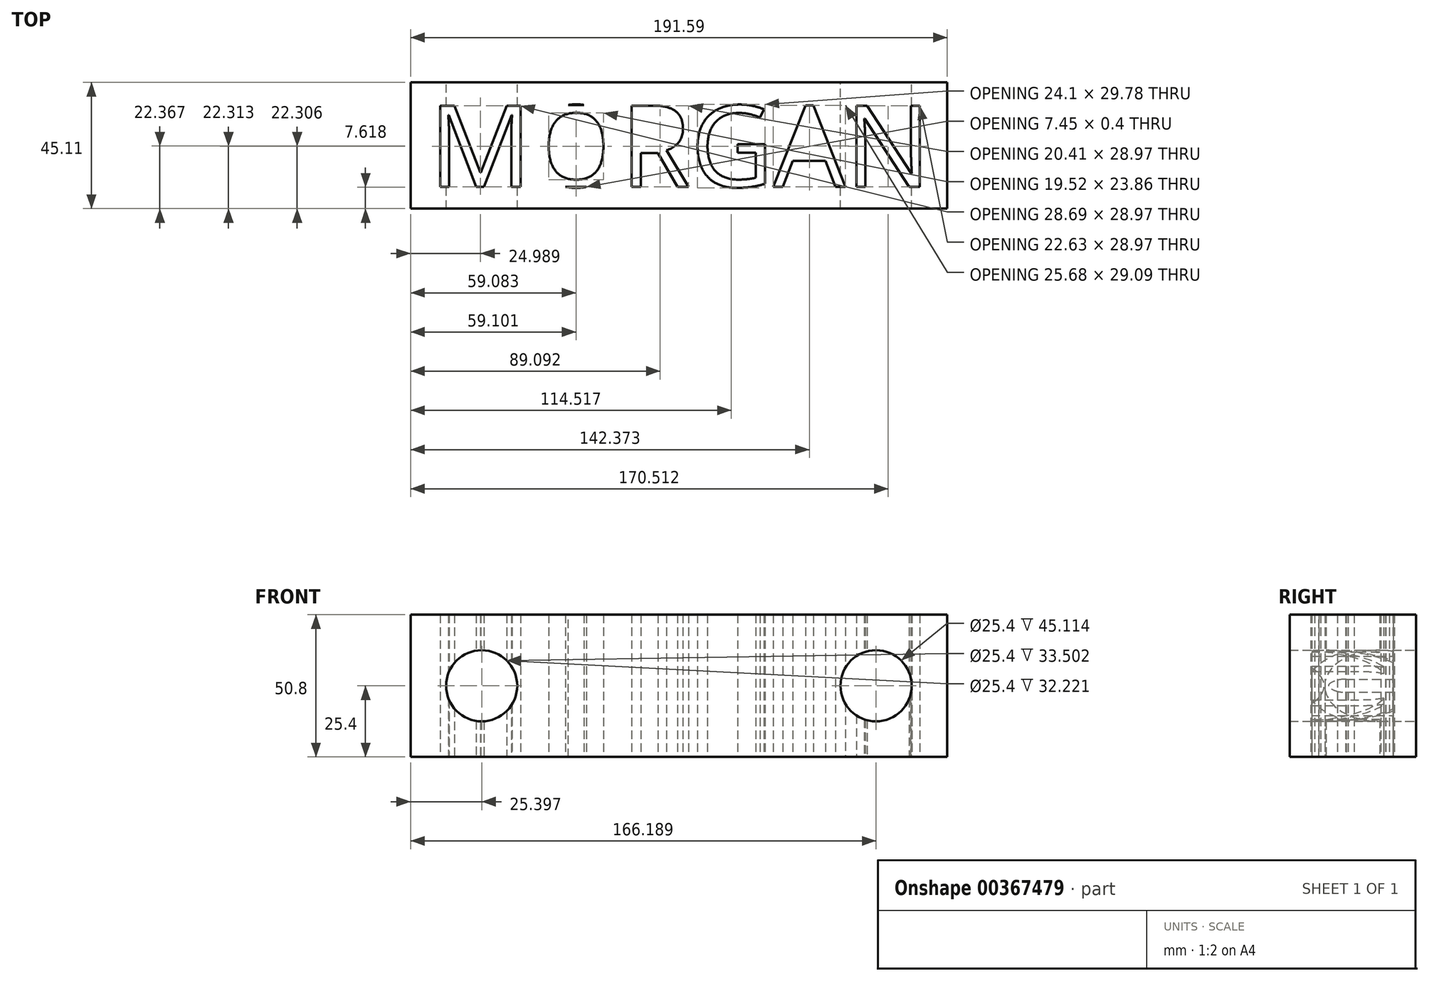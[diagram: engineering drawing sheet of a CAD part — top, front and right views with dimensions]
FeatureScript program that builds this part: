
annotation { "Feature Type Name" : "Feature", "Feature Type Description" : "" }
export const myFeature = defineFeature(function(context is Context, id is Id, definition is map)
    precondition{}
    {
        {
            var Q0;
            Q0=qCreatedBy(makeId("Top.planeOp"),FACE);
            var sketch = newSketch(context, id + "F0", { "sketchPlane" : qUnion([Q0])});
            skText(sketch, "E0", { "text": "MORGAN", "fontName": "OpenSans-Regular.ttf"});
            skLineSegment(sketch, "E1.bottom", {"start": v(105.15, -1.48) * mm, "end": v(282.95, -1.48) * mm});
            skLineSegment(sketch, "E1.top", {"start": v(105.15, -30.7) * mm, "end": v(282.95, -30.7) * mm});
            skLineSegment(sketch, "E1.left", {"start": v(105.15, -1.48) * mm, "end": v(105.15, -30.7) * mm});
            skLineSegment(sketch, "E1.right", {"start": v(282.95, -1.48) * mm, "end": v(282.95, -30.7) * mm});
            skLineSegment(sketch, "E2.bottom", {"start": v(98.49, 6.6) * mm, "end": v(290.08, 6.6) * mm});
            skLineSegment(sketch, "E2.top", {"start": v(98.49, -38.52) * mm, "end": v(290.08, -38.52) * mm});
            skLineSegment(sketch, "E2.left", {"start": v(98.49, 6.6) * mm, "end": v(98.49, -38.52) * mm});
            skLineSegment(sketch, "E2.right", {"start": v(290.08, 6.6) * mm, "end": v(290.08, -38.52) * mm});
            const initialGuessF0  = {"E0": [0.10515, -0.0307, 1, 0, 0.02922]};
            skSetInitialGuess(sketch, initialGuessF0);
            skSolve(sketch);
        }
        {
            var Q0;
            {var subQ2=sQuery(id+"F0.wireOp",EDGE,"E0.sketch_text.stroke-18");Q0=makeQuery(id+"F0.imprint","IMPRINT",FACE,{"disambiguationData":[TD([[makeQuery(id+"F0.imprint","IMPRINT",EDGE,{"derivedFrom":subQ2}),1.0]])]});}
            var Q1;
            {var subQ6=sQuery(id+"F0.wireOp",EDGE,"E0.sketch_text.stroke-5");Q1=makeQuery(id+"F0.imprint","IMPRINT",FACE,{"disambiguationData":[TD([[makeQuery(id+"F0.imprint","IMPRINT",EDGE,{"derivedFrom":subQ6}),1.0]])]});}
            var Q2;
            {var subQ1=sQuery(id+"F0.wireOp",EDGE,"E0.sketch_text.stroke-0");Q2=makeQuery(id+"F0.imprint","IMPRINT",FACE,{"disambiguationData":[TD([[makeQuery(id+"F0.imprint","IMPRINT",EDGE,{"derivedFrom":subQ1}),1.0]])]});}
            var Q3;
            {var subQ1=sQuery(id+"F0.wireOp",EDGE,"E0.sketch_text.stroke-13");Q3=makeQuery(id+"F0.imprint","IMPRINT",FACE,{"disambiguationData":[TD([[makeQuery(id+"F0.imprint","IMPRINT",EDGE,{"derivedFrom":subQ1}),1.0]])]});}
            var Q4;
            Q4=makeQuery(id+"F0.imprint","IMPRINT",FACE,{"disambiguationData":[TD([[makeQuery(id+"F0.imprint","IMPRINT",EDGE,{"derivedFrom":sQuery(id+"F0.wireOp",EDGE,"E0.sketch_text.stroke-52")}),1.0]])]});
            var Q5;
            {var subQ1=sQuery(id+"F0.wireOp",EDGE,"E0.sketch_text.stroke-86");Q5=makeQuery(id+"F0.imprint","IMPRINT",FACE,{"disambiguationData":[TD([[makeQuery(id+"F0.imprint","IMPRINT",EDGE,{"derivedFrom":subQ1}),1.0]])]});}
            var Q6;
            {var subQ0=sQuery(id+"F0.wireOp",EDGE,"E0.sketch_text.stroke-72");Q6=makeQuery(id+"F0.imprint","IMPRINT",FACE,{"disambiguationData":[TD([[makeQuery(id+"F0.imprint","IMPRINT",EDGE,{"derivedFrom":subQ0}),1.0]])]});}
            var Q7;
            Q7=makeQuery(id+"F0.imprint","IMPRINT",FACE,{"disambiguationData":[TD([[makeQuery(id+"F0.imprint","IMPRINT",EDGE,{"derivedFrom":sQuery(id+"F0.wireOp",EDGE,"E0.sketch_text.stroke-80")}),1.0]])]});
            var Q8;
            {var subQ7=sQuery(id+"F0.wireOp",EDGE,"E0.sketch_text.stroke-18");Q8=makeQuery(id+"F0.imprint","IMPRINT",FACE,{"disambiguationData":[TD([[makeQuery(id+"F0.imprint","IMPRINT",EDGE,{"derivedFrom":subQ7}),-1.0]])]});}
            var Q9;
            {var subQ0=sQuery(id+"F0.wireOp",EDGE,"E0.sketch_text.stroke-34");Q9=makeQuery(id+"F0.imprint","IMPRINT",FACE,{"disambiguationData":[TD([[makeQuery(id+"F0.imprint","IMPRINT",EDGE,{"derivedFrom":subQ0}),1.0]])]});}
            var Q10;
            Q10=makeQuery(id+"F0.imprint","IMPRINT",FACE,{"disambiguationData":[TD([[makeQuery(id+"F0.imprint","IMPRINT",EDGE,{"derivedFrom":sQuery(id+"F0.wireOp",EDGE,"E0.sketch_text.stroke-45")}),1.0]])]});
            var Q11;
            {var subQ19=sQuery(id+"F0.wireOp",EDGE,"E0.sketch_text.stroke-55");Q11=makeQuery(id+"F0.imprint","IMPRINT",FACE,{"disambiguationData":[TD([[makeQuery(id+"F0.imprint","IMPRINT",EDGE,{"derivedFrom":subQ19}),1.0]])]});}
            extrude(context, id + "F1", {"entities" : qUnion([Q0, Q1, Q2, Q3, Q4, Q5, Q6, Q7, Q8, Q9, Q10, Q11]), "depth" : 50.8 * mm});
        }
        {
            var Q0;
            Q0=makeQuery(id+"F1.opExtrude","SWEPT_FACE",FACE,{"disambiguationData":[OSD([sQuery(id+"F0.wireOp",EDGE,"E2.bottom")])]});
            var sketch = newSketch(context, id + "F2", { "sketchPlane" : qUnion([Q0])});
            skLineSegment(sketch, "E3.bottom", {"start": v(-290.08, 50.8) * mm, "end": v(-98.49, 50.8) * mm});
            skLineSegment(sketch, "E3.top", {"start": v(-290.08, 0) * mm, "end": v(-98.49, 0) * mm});
            skLineSegment(sketch, "E3.left", {"start": v(-290.08, 50.8) * mm, "end": v(-290.08, 0) * mm});
            skLineSegment(sketch, "E3.right", {"start": v(-98.49, 50.8) * mm, "end": v(-98.49, 0) * mm});
            skPoint(sketch, "E4", {"position": v(-123.89, 25.4) * mm});
            skPoint(sketch, "E5", {"position": v(-264.68, 25.4) * mm});
            skSolve(sketch);
        }
        {
            var Q0;
            Q0=sQuery(id+"F2.wireOp",VERTEX,"E4");
            var Q1;
            Q1=sQuery(id+"F2.wireOp",VERTEX,"E5");
            var Q2;
            Q2=makeQuery(id+"F1.opExtrude","SWEPT_BODY",BODY,{"disambiguationData":[OSD([sQuery(id+"F0.wireOp",EDGE,"E0.sketch_text.stroke-0"),sQuery(id+"F0.wireOp",EDGE,"E0.sketch_text.stroke-1"),sQuery(id+"F0.wireOp",EDGE,"E0.sketch_text.stroke-2"),sQuery(id+"F0.wireOp",EDGE,"E0.sketch_text.stroke-3"),sQuery(id+"F0.wireOp",EDGE,"E0.sketch_text.stroke-5"),sQuery(id+"F0.wireOp",EDGE,"E0.sketch_text.stroke-6"),sQuery(id+"F0.wireOp",EDGE,"E0.sketch_text.stroke-7"),sQuery(id+"F0.wireOp",EDGE,"E0.sketch_text.stroke-8"),sQuery(id+"F0.wireOp",EDGE,"E0.sketch_text.stroke-9"),sQuery(id+"F0.wireOp",EDGE,"E0.sketch_text.stroke-10"),sQuery(id+"F0.wireOp",EDGE,"E0.sketch_text.stroke-11"),sQuery(id+"F0.wireOp",EDGE,"E0.sketch_text.stroke-13"),sQuery(id+"F0.wireOp",EDGE,"E0.sketch_text.stroke-14"),sQuery(id+"F0.wireOp",EDGE,"E0.sketch_text.stroke-15"),sQuery(id+"F0.wireOp",EDGE,"E0.sketch_text.stroke-16"),sQuery(id+"F0.wireOp",EDGE,"E0.sketch_text.stroke-19"),sQuery(id+"F0.wireOp",EDGE,"E0.sketch_text.stroke-20"),sQuery(id+"F0.wireOp",EDGE,"E0.sketch_text.stroke-23"),sQuery(id+"F0.wireOp",EDGE,"E0.sketch_text.stroke-24"),sQuery(id+"F0.wireOp",EDGE,"E0.sketch_text.stroke-26"),sQuery(id+"F0.wireOp",EDGE,"E0.sketch_text.stroke-27"),sQuery(id+"F0.wireOp",EDGE,"E0.sketch_text.stroke-28"),sQuery(id+"F0.wireOp",EDGE,"E0.sketch_text.stroke-29"),sQuery(id+"F0.wireOp",EDGE,"E0.sketch_text.stroke-30"),sQuery(id+"F0.wireOp",EDGE,"E0.sketch_text.stroke-31"),sQuery(id+"F0.wireOp",EDGE,"E0.sketch_text.stroke-32"),sQuery(id+"F0.wireOp",EDGE,"E0.sketch_text.stroke-33"),sQuery(id+"F0.wireOp",EDGE,"E0.sketch_text.stroke-34"),sQuery(id+"F0.wireOp",EDGE,"E0.sketch_text.stroke-36"),sQuery(id+"F0.wireOp",EDGE,"E0.sketch_text.stroke-37"),sQuery(id+"F0.wireOp",EDGE,"E0.sketch_text.stroke-38"),sQuery(id+"F0.wireOp",EDGE,"E0.sketch_text.stroke-39"),sQuery(id+"F0.wireOp",EDGE,"E0.sketch_text.stroke-40"),sQuery(id+"F0.wireOp",EDGE,"E0.sketch_text.stroke-41"),sQuery(id+"F0.wireOp",EDGE,"E0.sketch_text.stroke-43"),sQuery(id+"F0.wireOp",EDGE,"E0.sketch_text.stroke-44"),sQuery(id+"F0.wireOp",EDGE,"E0.sketch_text.stroke-52"),sQuery(id+"F0.wireOp",EDGE,"E0.sketch_text.stroke-53"),sQuery(id+"F0.wireOp",EDGE,"E0.sketch_text.stroke-54"),sQuery(id+"F0.wireOp",EDGE,"E0.sketch_text.stroke-55"),sQuery(id+"F0.wireOp",EDGE,"E0.sketch_text.stroke-56"),sQuery(id+"F0.wireOp",EDGE,"E0.sketch_text.stroke-57"),sQuery(id+"F0.wireOp",EDGE,"E0.sketch_text.stroke-58"),sQuery(id+"F0.wireOp",EDGE,"E0.sketch_text.stroke-59"),sQuery(id+"F0.wireOp",EDGE,"E0.sketch_text.stroke-60"),sQuery(id+"F0.wireOp",EDGE,"E0.sketch_text.stroke-61"),sQuery(id+"F0.wireOp",EDGE,"E0.sketch_text.stroke-62"),sQuery(id+"F0.wireOp",EDGE,"E0.sketch_text.stroke-63"),sQuery(id+"F0.wireOp",EDGE,"E0.sketch_text.stroke-64"),sQuery(id+"F0.wireOp",EDGE,"E0.sketch_text.stroke-65"),sQuery(id+"F0.wireOp",EDGE,"E0.sketch_text.stroke-66"),sQuery(id+"F0.wireOp",EDGE,"E0.sketch_text.stroke-67"),sQuery(id+"F0.wireOp",EDGE,"E0.sketch_text.stroke-68"),sQuery(id+"F0.wireOp",EDGE,"E0.sketch_text.stroke-69"),sQuery(id+"F0.wireOp",EDGE,"E0.sketch_text.stroke-70"),sQuery(id+"F0.wireOp",EDGE,"E0.sketch_text.stroke-71"),sQuery(id+"F0.wireOp",EDGE,"E0.sketch_text.stroke-72"),sQuery(id+"F0.wireOp",EDGE,"E0.sketch_text.stroke-73"),sQuery(id+"F0.wireOp",EDGE,"E0.sketch_text.stroke-74"),sQuery(id+"F0.wireOp",EDGE,"E0.sketch_text.stroke-76"),sQuery(id+"F0.wireOp",EDGE,"E0.sketch_text.stroke-77"),sQuery(id+"F0.wireOp",EDGE,"E0.sketch_text.stroke-78"),sQuery(id+"F0.wireOp",EDGE,"E0.sketch_text.stroke-86"),sQuery(id+"F0.wireOp",EDGE,"E0.sketch_text.stroke-87"),sQuery(id+"F0.wireOp",EDGE,"E0.sketch_text.stroke-88"),sQuery(id+"F0.wireOp",EDGE,"E0.sketch_text.stroke-89"),sQuery(id+"F0.wireOp",EDGE,"E0.sketch_text.stroke-91"),sQuery(id+"F0.wireOp",EDGE,"E0.sketch_text.stroke-92"),sQuery(id+"F0.wireOp",EDGE,"E0.sketch_text.stroke-93"),sQuery(id+"F0.wireOp",EDGE,"E0.sketch_text.stroke-94"),sQuery(id+"F0.wireOp",EDGE,"E0.sketch_text.stroke-95"),sQuery(id+"F0.wireOp",EDGE,"E0.sketch_text.stroke-96"),sQuery(id+"F0.wireOp",EDGE,"E0.sketch_text.stroke-97"),sQuery(id+"F0.wireOp",EDGE,"E0.sketch_text.stroke-98"),sQuery(id+"F0.wireOp",EDGE,"E0.sketch_text.stroke-99"),sQuery(id+"F0.wireOp",EDGE,"E1.bottom"),sQuery(id+"F0.wireOp",EDGE,"E1.top"),sQuery(id+"F0.wireOp",EDGE,"E2.bottom"),sQuery(id+"F0.wireOp",EDGE,"E2.top"),sQuery(id+"F0.wireOp",EDGE,"E2.left"),sQuery(id+"F0.wireOp",EDGE,"E2.right")])]});
            hole(context, id + "F3", {"style" : HoleStyle.SIMPLE, "endStyle" : HoleEndStyle.THROUGH, "holeDiameter" : 25.4 * mm, "isTappedThrough" : true, "tappedDepth" : 12.7 * mm, "tapClearance" : 3, "locations" : qUnion([Q0, Q1]), "scope" : qUnion([Q2])});
        }
        {
            var Q0;
            Q0=makeQuery(id+"F1.opExtrude","SWEPT_BODY",BODY,{"disambiguationData":[OSD([sQuery(id+"F0.wireOp",EDGE,"E0.sketch_text.stroke-45"),sQuery(id+"F0.wireOp",EDGE,"E0.sketch_text.stroke-46"),sQuery(id+"F0.wireOp",EDGE,"E0.sketch_text.stroke-47"),sQuery(id+"F0.wireOp",EDGE,"E0.sketch_text.stroke-48"),sQuery(id+"F0.wireOp",EDGE,"E0.sketch_text.stroke-49"),sQuery(id+"F0.wireOp",EDGE,"E0.sketch_text.stroke-50"),sQuery(id+"F0.wireOp",EDGE,"E0.sketch_text.stroke-51")])]});
            deleteBodies(context, id + "F4", {"entities" : qUnion([Q0])});
        }
        {
            var Q0;
            Q0=makeQuery(id+"F1.opExtrude","SWEPT_BODY",BODY,{"disambiguationData":[OSD([sQuery(id+"F0.wireOp",EDGE,"E0.sketch_text.stroke-80"),sQuery(id+"F0.wireOp",EDGE,"E0.sketch_text.stroke-81"),sQuery(id+"F0.wireOp",EDGE,"E0.sketch_text.stroke-82"),sQuery(id+"F0.wireOp",EDGE,"E0.sketch_text.stroke-83"),sQuery(id+"F0.wireOp",EDGE,"E0.sketch_text.stroke-84")])]});
            deleteBodies(context, id + "F5", {"entities" : qUnion([Q0])});
        }
    });
